# Revit family: Haworth_Composites_Chair_ArcArm
name_source: partatom
category: Furniture
revit_build: Autodesk Revit 2018 (Build: 20170223_1515(x64)
units: mm (PartAtom-declared; Revit-internal decimal feet)

## family parameters
Always vertical = Yes
Cut with Voids When Loaded = No
OmniClass Number = 23.40.70.14.64.11
OmniClass Title = Office Furniture
Room Calculation Point = No
Shared = No
Work Plane-Based = No

## types (3) — shared parameters
Actual Depth = 23"
Actual Height = 33 3/4"
Actual Width = 22 3/8"
Assembly Code = E2020200
Glide Finish = Haworth _ Polymer _ Black
Manufacturer = Haworth
Model = Haworth Composites Chair
Revision Number = 1
Size = Verify Final Dim. w/ Haworth
Sustainability Info = http://www.haworth.com
URL = http://www.haworth.com
URL - Product = http://www.haworth.com
Warranty = http://www.haworth.com

## per-type parameters (varying)
| type | Back Control | Circle Back | Circle Back Control | Description | Slat Back | Slat Void Control | Upholstered Back |
| 4045-00 - Arc Arm - Upholstered Back | No | No | 1 1/2" | Haworth Composites Chair Arc Arm Upholstered Back | No | 1" | Yes |
| 4145-00 - Arc Arm - Circle Back | Yes | Yes | 17" | Haworth Composites Chair Arc Arm Circle Back | No | 1" | No |
| 4245-00 - Arc Arm - Slat Back | Yes | No | 1 1/2" | Haworth Composites Chair Arc Arm Slat Back | Yes | 20" | No |

## geometry (parser evidence)
native form markers: Sweep x2
no freeform markers — native parametric forms only
